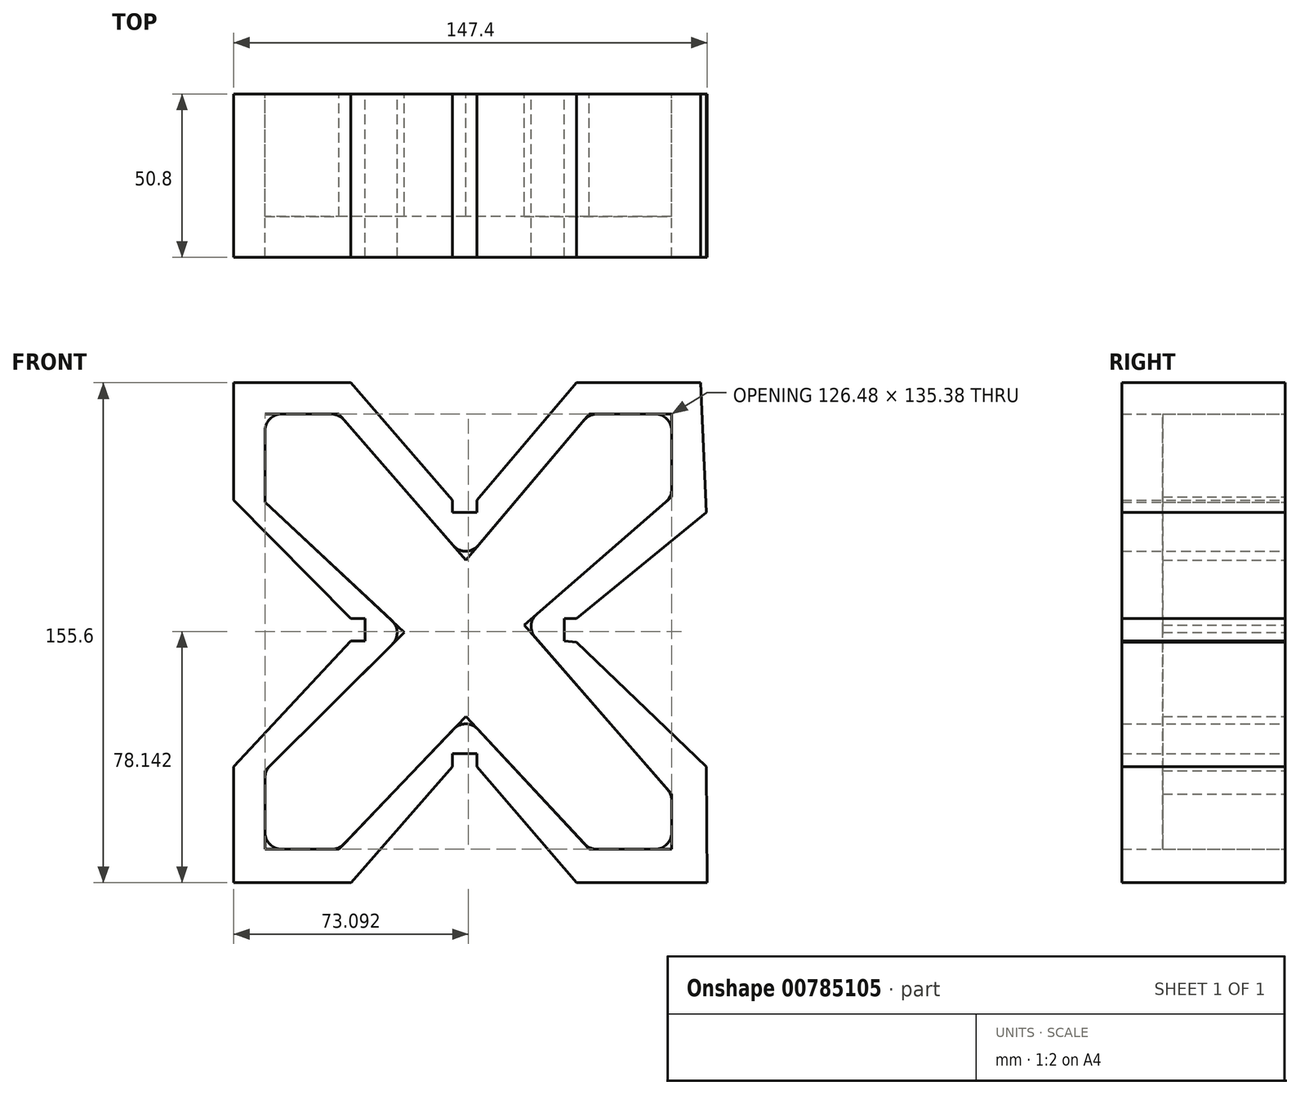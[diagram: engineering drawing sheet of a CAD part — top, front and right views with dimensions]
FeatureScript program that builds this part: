
annotation { "Feature Type Name" : "Feature", "Feature Type Description" : "" }
export const myFeature = defineFeature(function(context is Context, id is Id, definition is map)
    precondition{}
    {
        {
            var Q0;
            Q0=qCreatedBy(makeId("Front.planeOp"),FACE);
            var sketch = newSketch(context, id + "F0", { "sketchPlane" : qUnion([Q0])});
            skLineSegment(sketch, "E0", {"start": v(0, 0) * mm, "end": v(36.57, 0) * mm});
            skLineSegment(sketch, "E1", {"start": v(36.57, 0) * mm, "end": v(0, 0) * mm});
            skLineSegment(sketch, "E2", {"start": v(0, 0) * mm, "end": v(0, -36.58) * mm});
            skLineSegment(sketch, "E3", {"start": v(0, -119.51) * mm, "end": v(0, -155.6) * mm});
            skLineSegment(sketch, "E4", {"start": v(0, -155.6) * mm, "end": v(36.69, -155.6) * mm});
            skLineSegment(sketch, "E5", {"start": v(36.69, -155.6) * mm, "end": v(68.15, -119.51) * mm});
            skLineSegment(sketch, "E6", {"start": v(68.15, -119.51) * mm, "end": v(68.15, -115.36) * mm});
            skLineSegment(sketch, "E7", {"start": v(68.15, -115.36) * mm, "end": v(75.8, -115.36) * mm});
            skLineSegment(sketch, "E8", {"start": v(75.8, -115.36) * mm, "end": v(75.8, -119.51) * mm});
            skLineSegment(sketch, "E9", {"start": v(75.8, -119.51) * mm, "end": v(106.75, -155.6) * mm});
            skLineSegment(sketch, "E10", {"start": v(36.57, 0) * mm, "end": v(68.15, -36.58) * mm});
            skPoint(sketch, "E11.end.orphan", {"position": v(75.8, -36.58) * mm});
            skLineSegment(sketch, "E12", {"start": v(68.15, -36.58) * mm, "end": v(68.15, -40.32) * mm});
            skLineSegment(sketch, "E13", {"start": v(75.8, -40.32) * mm, "end": v(68.15, -40.32) * mm});
            skLineSegment(sketch, "E14", {"start": v(75.8, -36.58) * mm, "end": v(75.8, -40.32) * mm});
            skLineSegment(sketch, "E15", {"start": v(75.8, -36.58) * mm, "end": v(106.75, 0) * mm});
            skLineSegment(sketch, "E16", {"start": v(106.75, 0) * mm, "end": v(145.4, 0) * mm});
            skLineSegment(sketch, "E17", {"start": v(147.06, -40.32) * mm, "end": v(106.75, -73.37) * mm});
            skLineSegment(sketch, "E18", {"start": v(106.75, -73.37) * mm, "end": v(102.95, -73.37) * mm});
            skLineSegment(sketch, "E19", {"start": v(102.95, -73.37) * mm, "end": v(102.95, -80.38) * mm});
            skLineSegment(sketch, "E20", {"start": v(106.75, -80.76) * mm, "end": v(147.06, -119.51) * mm});
            skLineSegment(sketch, "E21", {"start": v(106.75, -155.6) * mm, "end": v(147.4, -155.6) * mm});
            skLineSegment(sketch, "E22", {"start": v(0, -36.58) * mm, "end": v(36.57, -73.37) * mm});
            skLineSegment(sketch, "E23", {"start": v(36.57, -73.37) * mm, "end": v(40.92, -73.37) * mm});
            skLineSegment(sketch, "E24", {"start": v(40.92, -73.37) * mm, "end": v(40.92, -80.37) * mm});
            skLineSegment(sketch, "E25", {"start": v(40.92, -80.37) * mm, "end": v(36.57, -80.37) * mm});
            skLineSegment(sketch, "E26", {"start": v(0, -119.51) * mm, "end": v(36.57, -80.37) * mm});
            skLineSegment(sketch, "E27", {"start": v(145.4, 0) * mm, "end": v(147.06, -40.32) * mm});
            skLineSegment(sketch, "E28", {"start": v(147.4, -155.6) * mm, "end": v(147.06, -119.51) * mm});
            skLineSegment(sketch, "E29", {"start": v(102.95, -80.38) * mm, "end": v(106.75, -80.76) * mm});
            skLineSegment(sketch, "E30", {"start": v(9.85, -9.77) * mm, "end": v(32.83, -9.77) * mm});
            skLineSegment(sketch, "E31", {"start": v(32.83, -9.77) * mm, "end": v(72.3, -55.18) * mm});
            skLineSegment(sketch, "E32", {"start": v(72.3, -55.18) * mm, "end": v(110.73, -9.77) * mm});
            skLineSegment(sketch, "E33", {"start": v(110.73, -9.77) * mm, "end": v(136.33, -9.77) * mm});
            skLineSegment(sketch, "E34", {"start": v(136.33, -9.77) * mm, "end": v(136.33, -35.56) * mm});
            skLineSegment(sketch, "E35", {"start": v(136.33, -35.56) * mm, "end": v(90.54, -75.36) * mm});
            skLineSegment(sketch, "E36", {"start": v(90.54, -75.36) * mm, "end": v(136.33, -128.03) * mm});
            skLineSegment(sketch, "E37", {"start": v(136.33, -128.03) * mm, "end": v(136.33, -145.15) * mm});
            skLineSegment(sketch, "E38", {"start": v(136.33, -145.15) * mm, "end": v(110.73, -145.15) * mm});
            skLineSegment(sketch, "E39", {"start": v(110.73, -145.15) * mm, "end": v(72.3, -103.85) * mm});
            skLineSegment(sketch, "E40", {"start": v(72.3, -103.85) * mm, "end": v(32.83, -145.15) * mm});
            skLineSegment(sketch, "E41", {"start": v(32.83, -145.15) * mm, "end": v(9.85, -145.15) * mm});
            skLineSegment(sketch, "E42", {"start": v(9.85, -145.15) * mm, "end": v(9.85, -120.7) * mm});
            skLineSegment(sketch, "E43", {"start": v(9.85, -120.7) * mm, "end": v(53.18, -77.65) * mm});
            skLineSegment(sketch, "E44", {"start": v(53.18, -77.65) * mm, "end": v(9.85, -37.17) * mm});
            skLineSegment(sketch, "E45", {"start": v(9.85, -37.17) * mm, "end": v(9.85, -9.77) * mm});
            skSolve(sketch);
        }
        {
            var Q0;
            Q0 = qSketchRegion(id + "F0", true);
            extrude(context, id + "F1", {"entities" : qUnion([Q0]), "depth" : 50.8 * mm, "offsetDistance" : 25.4 * mm});
        }
        {
            var Q0;
            Q0=makeQuery(id+"F0.imprint","IMPRINT",FACE,{"disambiguationData":[TD([[makeQuery(id+"F0.imprint","IMPRINT",EDGE,{"derivedFrom":sQuery(id+"F0.wireOp",EDGE,"E30")}),-1.0]])]});
            extrude(context, id + "F2", {"entities" : qUnion([Q0]), "depth" : 38.1 * mm, "offsetDistance" : 25.4 * mm});
        }
        {
            var Q0;
            Q0=makeQuery(id+"F1.opExtrude","SWEPT_EDGE",EDGE,{"disambiguationData":[OSD([sQuery(id+"F0.wireOp",EDGE,"E30"),sQuery(id+"F0.wireOp",EDGE,"E45")])]});
            var Q1;
            Q1=makeQuery(id+"F1.opExtrude","SWEPT_EDGE",EDGE,{"disambiguationData":[OSD([sQuery(id+"F0.wireOp",EDGE,"E30"),sQuery(id+"F0.wireOp",EDGE,"E31")])]});
            var Q2;
            Q2=makeQuery(id+"F1.opExtrude","SWEPT_EDGE",EDGE,{"disambiguationData":[OSD([sQuery(id+"F0.wireOp",EDGE,"E43"),sQuery(id+"F0.wireOp",EDGE,"E44")])]});
            var Q3;
            Q3=makeQuery(id+"F1.opExtrude","SWEPT_EDGE",EDGE,{"disambiguationData":[OSD([sQuery(id+"F0.wireOp",EDGE,"E31"),sQuery(id+"F0.wireOp",EDGE,"E32")])]});
            var Q4;
            Q4=makeQuery(id+"F1.opExtrude","SWEPT_EDGE",EDGE,{"disambiguationData":[OSD([sQuery(id+"F0.wireOp",EDGE,"E32"),sQuery(id+"F0.wireOp",EDGE,"E33")])]});
            var Q5;
            Q5=makeQuery(id+"F1.opExtrude","SWEPT_EDGE",EDGE,{"disambiguationData":[OSD([sQuery(id+"F0.wireOp",EDGE,"E33"),sQuery(id+"F0.wireOp",EDGE,"E34")])]});
            var Q6;
            Q6=makeQuery(id+"F1.opExtrude","SWEPT_EDGE",EDGE,{"disambiguationData":[OSD([sQuery(id+"F0.wireOp",EDGE,"E34"),sQuery(id+"F0.wireOp",EDGE,"E35")])]});
            var Q7;
            Q7=makeQuery(id+"F1.opExtrude","SWEPT_EDGE",EDGE,{"disambiguationData":[OSD([sQuery(id+"F0.wireOp",EDGE,"E35"),sQuery(id+"F0.wireOp",EDGE,"E36")])]});
            var Q8;
            Q8=makeQuery(id+"F1.opExtrude","SWEPT_EDGE",EDGE,{"disambiguationData":[OSD([sQuery(id+"F0.wireOp",EDGE,"E42"),sQuery(id+"F0.wireOp",EDGE,"E43")])]});
            var Q9;
            Q9=makeQuery(id+"F1.opExtrude","SWEPT_EDGE",EDGE,{"disambiguationData":[OSD([sQuery(id+"F0.wireOp",EDGE,"E39"),sQuery(id+"F0.wireOp",EDGE,"E40")])]});
            var Q10;
            Q10=makeQuery(id+"F1.opExtrude","SWEPT_EDGE",EDGE,{"disambiguationData":[OSD([sQuery(id+"F0.wireOp",EDGE,"E38"),sQuery(id+"F0.wireOp",EDGE,"E39")])]});
            var Q11;
            Q11=makeQuery(id+"F1.opExtrude","SWEPT_EDGE",EDGE,{"disambiguationData":[OSD([sQuery(id+"F0.wireOp",EDGE,"E41"),sQuery(id+"F0.wireOp",EDGE,"E42")])]});
            var Q12;
            Q12=makeQuery(id+"F1.opExtrude","SWEPT_EDGE",EDGE,{"disambiguationData":[OSD([sQuery(id+"F0.wireOp",EDGE,"E40"),sQuery(id+"F0.wireOp",EDGE,"E41")])]});
            var Q13;
            Q13=makeQuery(id+"F1.opExtrude","SWEPT_EDGE",EDGE,{"disambiguationData":[OSD([sQuery(id+"F0.wireOp",EDGE,"E36"),sQuery(id+"F0.wireOp",EDGE,"E37")])]});
            var Q14;
            Q14=makeQuery(id+"F1.opExtrude","SWEPT_EDGE",EDGE,{"disambiguationData":[OSD([sQuery(id+"F0.wireOp",EDGE,"E37"),sQuery(id+"F0.wireOp",EDGE,"E38")])]});
            fillet(context, id + "F3", {"entities" : qUnion([Q0, Q1, Q2, Q3, Q4, Q5, Q6, Q7, Q8, Q9, Q10, Q11, Q12, Q13, Q14]), "radius" : 5.08 * mm, "tangentPropagation" : true, "allowEdgeOverflow" : false});
        }
    });
